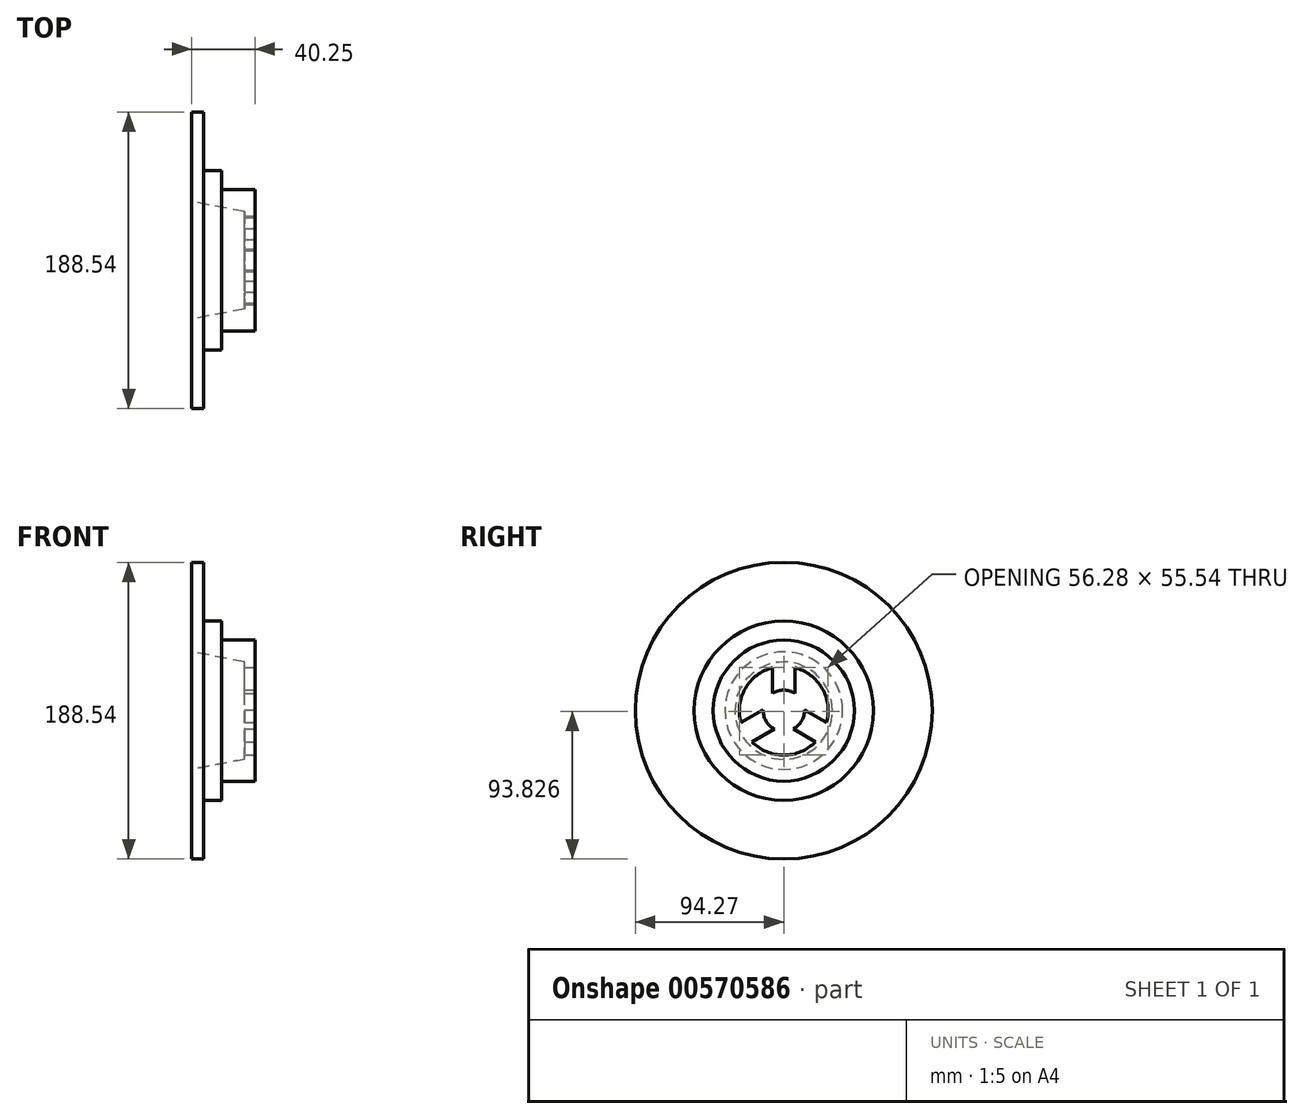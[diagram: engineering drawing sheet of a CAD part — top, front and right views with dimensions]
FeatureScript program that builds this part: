
annotation { "Feature Type Name" : "Feature", "Feature Type Description" : "" }
export const myFeature = defineFeature(function(context is Context, id is Id, definition is map)
    precondition{}
    {
        {
            var Q0;
            Q0=qCreatedBy(makeId("Front.planeOp"),FACE);
            var sketch = newSketch(context, id + "F0", { "sketchPlane" : qUnion([Q0])});
            skLineSegment(sketch, "E0", {"start": v(0, 122.6) * mm, "end": v(0, 94.27) * mm, "construction": true});
            skLineSegment(sketch, "E1", {"start": v(0, 0) * mm, "end": v(-182.32, 0) * mm, "construction": true});
            skLineSegment(sketch, "E2", {"start": v(0, 94.27) * mm, "end": v(7.4, 94.27) * mm});
            skLineSegment(sketch, "E3", {"start": v(7.4, 94.27) * mm, "end": v(7.4, 56.89) * mm});
            skLineSegment(sketch, "E4", {"start": v(7.4, 56.89) * mm, "end": v(19.1, 56.89) * mm});
            skLineSegment(sketch, "E5", {"start": v(19.1, 56.89) * mm, "end": v(19.1, 44.8) * mm});
            skLineSegment(sketch, "E6", {"start": v(19.1, 44.8) * mm, "end": v(40.25, 44.8) * mm});
            skLineSegment(sketch, "E7", {"start": v(40.25, 44.8) * mm, "end": v(40.25, 13.08) * mm});
            skLineSegment(sketch, "E8", {"start": v(40.25, 13.08) * mm, "end": v(33.54, 13.08) * mm});
            skLineSegment(sketch, "E9.trimOffspring", {"start": v(0, 13.08) * mm, "end": v(0, 0) * mm, "construction": true});
            skLineSegment(sketch, "E10", {"start": v(0, 94.27) * mm, "end": v(0, 37.33) * mm});
            skLineSegment(sketch, "E11", {"start": v(0, 37.33) * mm, "end": v(33.54, 30.94) * mm});
            skLineSegment(sketch, "E12", {"start": v(33.54, 30.94) * mm, "end": v(33.54, 13.08) * mm});
            skSolve(sketch);
        }
        {
            var Q0;
            Q0=makeQuery(id+"F0.imprint","IMPRINT",FACE,{"disambiguationData":[TD([[makeQuery(id+"F0.imprint","IMPRINT",EDGE,{"derivedFrom":sQuery(id+"F0.wireOp",EDGE,"E2")}),-1.0]])]});
            var Q1;
            Q1=sQuery(id+"F0.wireOp",EDGE,"E1");
            revolve(context, id + "F1", {"entities" : qUnion([Q0]), "axis" : qUnion([Q1]), "revolveType" : RevolveType.FULL});
        }
        {
            var Q0;
            Q0=makeQuery(id+"F1.opRevolve","SWEPT_FACE",FACE,{"disambiguationData":[OSD([sQuery(id+"F0.wireOp",EDGE,"E7")])]});
            var sketch = newSketch(context, id + "F2", { "sketchPlane" : qUnion([Q0])});
            skLineSegment(sketch, "E13", {"start": v(0, 89.3) * mm, "end": v(0, 0) * mm, "construction": true});
            skLineSegment(sketch, "E14", {"start": v(0, 0) * mm, "end": v(-135.92, 0) * mm, "construction": true});
            skLineSegment(sketch, "E15", {"start": v(-7.02, 27.33) * mm, "end": v(-7.02, 11.04) * mm});
            skLineSegment(sketch, "E16.MirrorCS", {"start": v(7.02, 27.33) * mm, "end": v(7.02, 11.04) * mm});
            skCircle(sketch, "E17", {"center": v(0, 0) * mm, "radius": 28.21 * mm});
            skCircle(sketch, "E18", {"center": v(0, 0) * mm, "radius": 13.08 * mm});
            skLineSegment(sketch, "E19.1.0", {"start": v(-20.16, -19.74) * mm, "end": v(-6.05, -11.6) * mm});
            skLineSegment(sketch, "E19.1.1", {"start": v(-27.18, -7.58) * mm, "end": v(-13.07, 0.56) * mm});
            skLineSegment(sketch, "E19.2.0", {"start": v(27.18, -7.58) * mm, "end": v(13.07, 0.56) * mm});
            skLineSegment(sketch, "E19.2.1", {"start": v(20.16, -19.74) * mm, "end": v(6.05, -11.6) * mm});
            skSolve(sketch);
        }
        {
            var Q0;
            {var subQ0=sQuery(id+"F2.wireOp",EDGE,"E15");Q0=makeQuery(id+"F2.imprint","IMPRINT",FACE,{"disambiguationData":[TD([[makeQuery(id+"F2.imprint","IMPRINT",EDGE,{"derivedFrom":subQ0}),-1.0]])]});}
            var Q1;
            {var subQ0=sQuery(id+"F2.wireOp",EDGE,"E19.1.0");Q1=makeQuery(id+"F2.imprint","IMPRINT",FACE,{"disambiguationData":[TD([[makeQuery(id+"F2.imprint","IMPRINT",EDGE,{"derivedFrom":subQ0}),-1.0]])]});}
            var Q2;
            {var subQ0=sQuery(id+"F2.wireOp",EDGE,"E16.MirrorCS");Q2=makeQuery(id+"F2.imprint","IMPRINT",FACE,{"disambiguationData":[TD([[makeQuery(id+"F2.imprint","IMPRINT",EDGE,{"derivedFrom":subQ0}),1.0]])]});}
            extrude(context, id + "F3", {"entities" : qUnion([Q0, Q1, Q2]), "operationType" : NewBodyOperationType.REMOVE, "endBound" : BoundingType.THROUGH_ALL, "oppositeDirection" : true, "depth" : 25 * mm, "offsetDistance" : 25 * mm});
        }
    });
